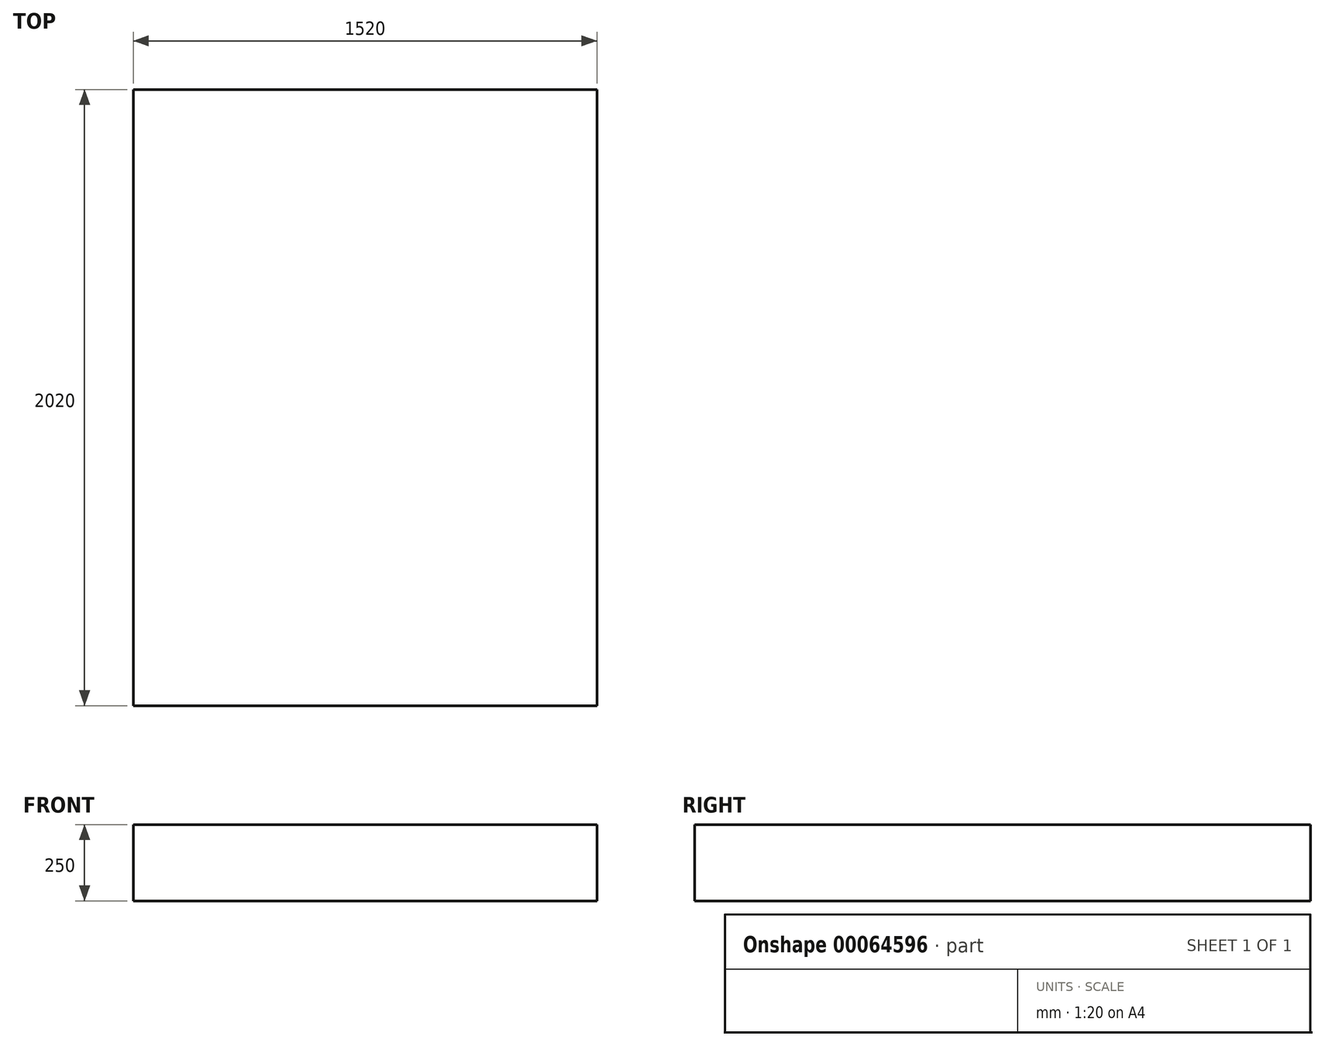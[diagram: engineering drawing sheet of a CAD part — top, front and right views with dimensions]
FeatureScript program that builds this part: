
annotation { "Feature Type Name" : "Feature", "Feature Type Description" : "" }
export const myFeature = defineFeature(function(context is Context, id is Id, definition is map)
    precondition{}
    {
        {
            var Q0;
            Q0=qCreatedBy(makeId("Top.planeOp"),FACE);
            var sketch = newSketch(context, id + "F0", { "sketchPlane" : qUnion([Q0])});
            skLineSegment(sketch, "E0.bottom", {"start": v(-118.81, 1912.55) * mm, "end": v(1401.19, 1912.55) * mm});
            skLineSegment(sketch, "E0.top", {"start": v(-118.81, -107.45) * mm, "end": v(1401.19, -107.45) * mm});
            skLineSegment(sketch, "E0.left", {"start": v(-118.81, 1912.55) * mm, "end": v(-118.81, -107.45) * mm});
            skLineSegment(sketch, "E0.right", {"start": v(1401.19, 1912.55) * mm, "end": v(1401.19, -107.45) * mm});
            skSolve(sketch);
        }
        {
            var Q0;
            Q0 = qSketchRegion(id + "F0", true);
            extrude(context, id + "F1", {"entities" : qUnion([Q0]), "depth" : 250 * mm});
        }
    });
